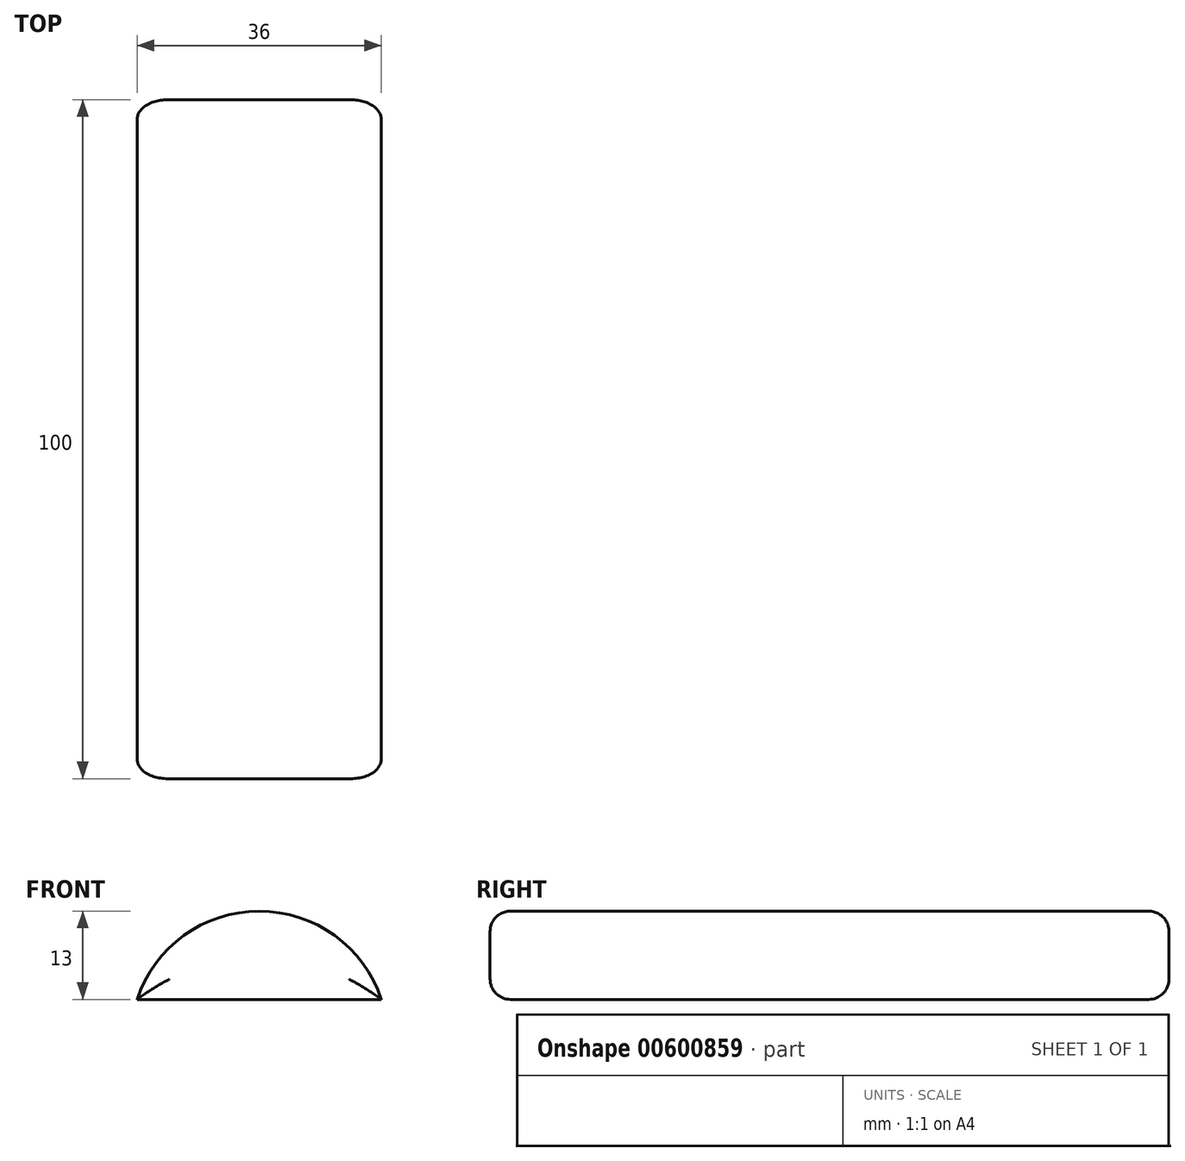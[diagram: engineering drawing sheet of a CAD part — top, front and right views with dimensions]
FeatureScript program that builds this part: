
annotation { "Feature Type Name" : "Feature", "Feature Type Description" : "" }
export const myFeature = defineFeature(function(context is Context, id is Id, definition is map)
    precondition{}
    {
        {
            var Q0;
            Q0=qCreatedBy(makeId("Front.planeOp"),FACE);
            var sketch = newSketch(context, id + "F0", { "sketchPlane" : qUnion([Q0])});
            skPoint(sketch, "E0.middle", {"position": v(0, 0) * mm});
            skLineSegment(sketch, "E1", {"start": v(-18, -7) * mm, "end": v(-18, -4) * mm});
            skLineSegment(sketch, "E2", {"start": v(18, -7) * mm, "end": v(18, -4) * mm});
            skLineSegment(sketch, "E3", {"start": v(-18, -7) * mm, "end": v(18, -7) * mm});
            skLineSegment(sketch, "E4", {"start": v(0, 0) * mm, "end": v(0, 9) * mm});
            skLineSegment(sketch, "E5", {"start": v(0, 0) * mm, "end": v(0, -7) * mm});
            skArc(sketch, "E6", {"start": v(18, -4) * mm, "mid": v(0, 9) * mm, "end": v(-18, -4) * mm});
            skLineSegment(sketch, "E7.bottom", {"start": v(-18, -4) * mm, "end": v(18, -4) * mm});
            skLineSegment(sketch, "E7.left", {"start": v(-18, -4) * mm, "end": v(-18, -7) * mm});
            skLineSegment(sketch, "E7.right", {"start": v(18, -4) * mm, "end": v(18, -7) * mm});
            skSolve(sketch);
        }
        {
            var Q0;
            {var subQ0=sQuery(id+"F0.wireOp",EDGE,"E4");Q0=makeQuery(id+"F0.imprint","IMPRINT",FACE,{"disambiguationData":[TD([[makeQuery(id+"F0.imprint","IMPRINT",EDGE,{"derivedFrom":subQ0}),1.0]])]});}
            var Q1;
            {var subQ0=sQuery(id+"F0.wireOp",EDGE,"E4");Q1=makeQuery(id+"F0.imprint","IMPRINT",FACE,{"disambiguationData":[TD([[makeQuery(id+"F0.imprint","IMPRINT",EDGE,{"derivedFrom":subQ0}),-1.0]])]});}
            var Q2;
            {var subQ5=sQuery(id+"F0.wireOp",EDGE,"E7.left");Q2=makeQuery(id+"F0.imprint","IMPRINT",FACE,{"disambiguationData":[TD([[makeQuery(id+"F0.imprint","IMPRINT",EDGE,{"derivedFrom":subQ5}),1.0]])]});}
            var Q3;
            {var subQ5=sQuery(id+"F0.wireOp",EDGE,"E7.right");Q3=makeQuery(id+"F0.imprint","IMPRINT",FACE,{"disambiguationData":[TD([[makeQuery(id+"F0.imprint","IMPRINT",EDGE,{"derivedFrom":subQ5}),-1.0]])]});}
            extrude(context, id + "F1", {"entities" : qUnion([Q0, Q1, Q2, Q3]), "depth" : 100 * mm, "offsetDistance" : 25 * mm});
        }
        {
            var Q0;
            Q0=makeQuery(id+"F1.opExtrude","CAP_FACE",FACE,{"disambiguationData":[OSD([sQuery(id+"F0.wireOp",EDGE,"E1"),sQuery(id+"F0.wireOp",EDGE,"E2"),sQuery(id+"F0.wireOp",EDGE,"E3"),sQuery(id+"F0.wireOp",EDGE,"E6")])],"isStart":false});
            var Q1;
            Q1=makeQuery(id+"F1.opExtrude","CAP_FACE",FACE,{"disambiguationData":[OSD([sQuery(id+"F0.wireOp",EDGE,"E6"),sQuery(id+"F0.wireOp",EDGE,"E3"),sQuery(id+"F0.wireOp",EDGE,"E7.left"),sQuery(id+"F0.wireOp",EDGE,"E7.right")])],"isStart":true});
            fillet(context, id + "F2", {"entities" : qUnion([Q0, Q1]), "radius" : 3 * mm, "tangentPropagation" : true, "allowEdgeOverflow" : false});
        }
    });
